# Revit family: 2-699-24 IO
name_source: partatom
category: Lighting Fixtures
revit_build: Autodesk Revit LT 2014 (Build: 20130308_1515(x64)
units: mm (PartAtom-declared; Revit-internal decimal feet)

## types (1)
- 2-699-24 IO
    Apparent Load = 53 VA
    Ballast Manufacturer = Fulham RHA-UNV-242-C
    Color Filter = 16777215
    Default Elevation = 4' - 0"
    Description = 17"dia. ceiling mount
    Diffuser = Matte White Acrylic
    Diffuser dia. = 1' - 3 1/8"
    Dimming Lamp Color Temperature Shift = <None>
    Emit Shape Visible in Rendering = No
    Emit from Circle Diameter = 2' - 0"
    Input Power = 52.5
    Input Power Factor = 0.99
    Input Voltage = 120
    Junction Box = 4" Octagonal
    Lamp = 1x22W, 1x40W T5 circline fluorescent
    Lamp Manufacturer = Sylvania
    Manufacturer = Oxygen Lighting
    Metal Finish = Sating Nickel
    Model = 2-699-24
    Photometric Web File = 2-699-24.IES
    Tilt Angle = -90.00°
    Type Comments = Lighitng- Fluoreescent
    URL = www.oxygenlighting.com

## geometry (parser evidence)
native form markers: Sweep x1
no freeform markers — native parametric forms only
